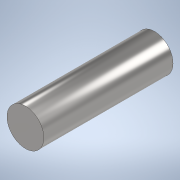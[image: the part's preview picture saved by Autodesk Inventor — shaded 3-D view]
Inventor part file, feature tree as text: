
AUTODESK INVENTOR PART (.ipt)
format: ipt  version: 2022 (Build 260153000, 153)  size: 98,816 bytes
history: native  units: in
note: dims shown in document units (in); Inventor stores cm internally (conversion verified against a paired STEP export)
features: extrude x1, sketch x1
ambient origin geometry x8: Origin, YZ Plane, XZ Plane, XY Plane, X Axis, Y Axis, Z Axis, Center Point
bodies: Solid1 (feature_tree)
feature tree (2):
  extrude  "Extrusion1"  Depth=2.7559in TaperAngle=0.0deg
  sketch  "Sketch1"  dims[d0=0.7874in d1=2.7559in d2=0.0in]
